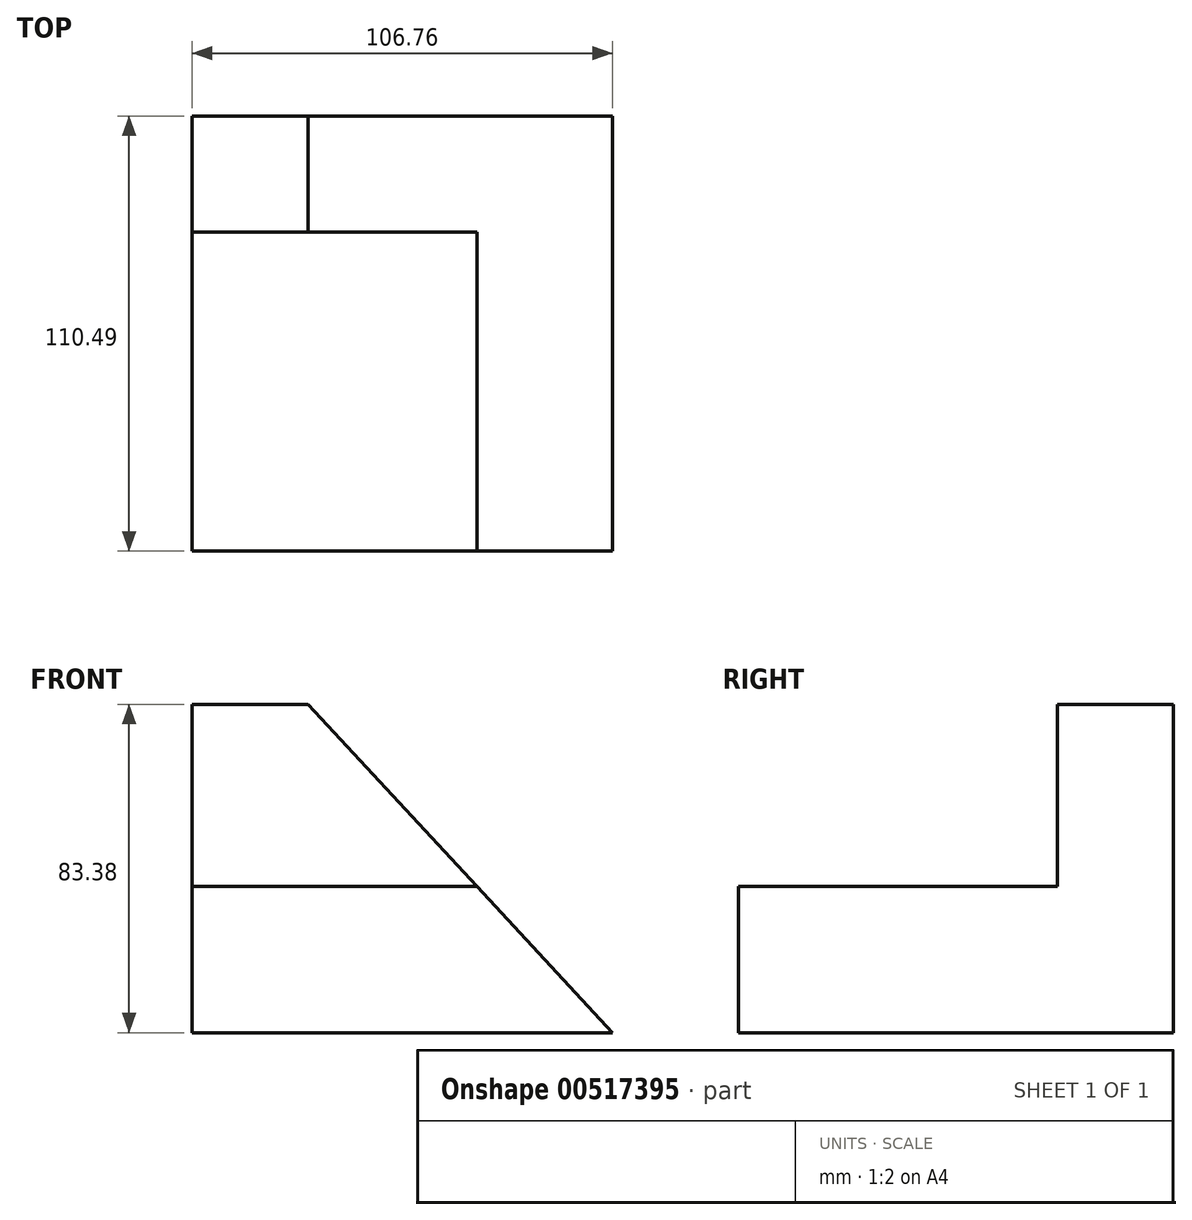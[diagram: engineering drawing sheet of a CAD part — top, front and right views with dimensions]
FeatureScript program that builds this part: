
annotation { "Feature Type Name" : "Feature", "Feature Type Description" : "" }
export const myFeature = defineFeature(function(context is Context, id is Id, definition is map)
    precondition{}
    {
        {
            var Q0;
            Q0=qCreatedBy(makeId("Front.planeOp"),FACE);
            var sketch = newSketch(context, id + "F0", { "sketchPlane" : qUnion([Q0])});
            skLineSegment(sketch, "E0", {"start": v(-58.56, -31.09) * mm, "end": v(-58.56, 53.98) * mm});
            skLineSegment(sketch, "E1", {"start": v(-58.56, 53.98) * mm, "end": v(-29.16, 53.98) * mm});
            skLineSegment(sketch, "E2", {"start": v(-29.16, 53.98) * mm, "end": v(48.2, -29.4) * mm});
            skLineSegment(sketch, "E3", {"start": v(48.2, -29.4) * mm, "end": v(-58.56, -29.4) * mm});
            skLineSegment(sketch, "E4", {"start": v(-58.56, 7.71) * mm, "end": v(13.77, 7.71) * mm});
            skSolve(sketch);
        }
        {
            var Q0;
            {var subQ0=sQuery(id+"F0.wireOp",EDGE,"E3");Q0=makeQuery(id+"F0.imprint","IMPRINT",FACE,{"disambiguationData":[TD([[makeQuery(id+"F0.imprint","IMPRINT",EDGE,{"derivedFrom":subQ0}),-1.0]])]});}
            extrude(context, id + "F1", {"entities" : qUnion([Q0]), "depth" : 110.49 * mm, "offsetDistance" : 25.4 * mm});
        }
        {
            var Q0;
            Q0 = qSketchRegion(id + "F0", true);
            extrude(context, id + "F2", {"entities" : qUnion([Q0]), "operationType" : NewBodyOperationType.ADD, "depth" : 29.46 * mm, "offsetDistance" : 25.4 * mm});
        }
    });
